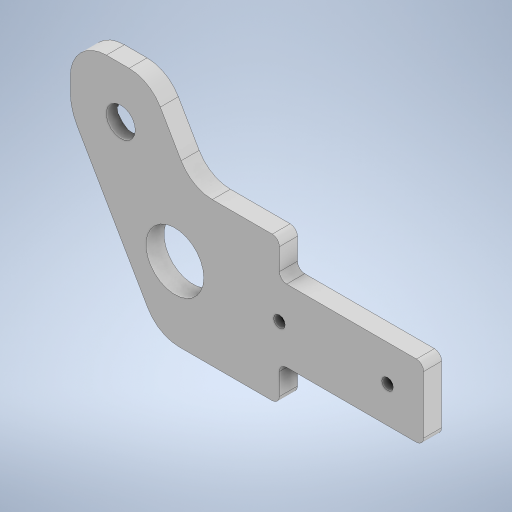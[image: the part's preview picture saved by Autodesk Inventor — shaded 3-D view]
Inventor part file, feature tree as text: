
AUTODESK INVENTOR PART (.ipt)
format: ipt  version: 2024.3 (Build 283343000, 343)  size: 315,904 bytes
history: native  units: mm
features: sketch x4, extrude x3, fillet x2, other x1, hole x1
ambient origin geometry x8: Origin, YZ Plane, XZ Plane, XY Plane, X Axis, Y Axis, Z Axis, Center Point
bodies: Body1 (feature_tree)
feature tree (11):
  other  "ソリッド1"
  extrude  "押し出し1"  Depth=98.0mm
  hole  "穴1"  [1 undecoded]
  fillet  "フィレット1"  Radius=40.0mm
  fillet  "フィレット2"  Radius=20.0mm
  extrude  "押し出し3"  Depth=10.0mm
  extrude  "押し出し4"  Depth=69.0mm
  sketch  "スケッチ1"
  sketch  "スケッチ2"
  sketch  "スケッチ5"
  sketch  "スケッチ6"
note: 1 required parameter value undecoded (feature->parameter linkage not recoverable at this tier; creation-order binding heuristic only, values carry confidence <= 0.55)
